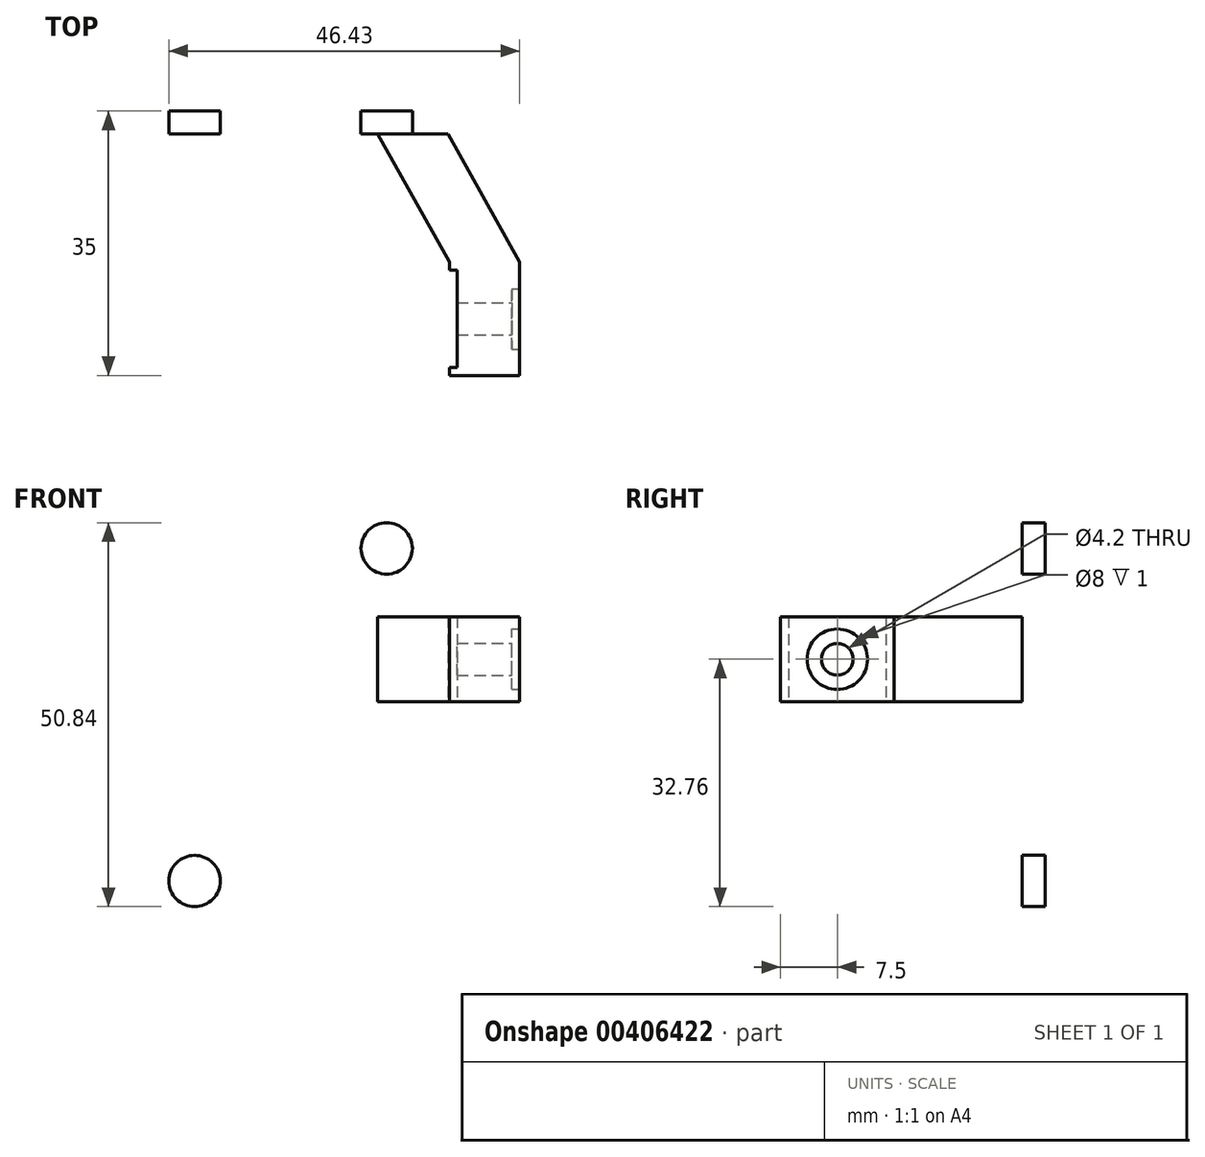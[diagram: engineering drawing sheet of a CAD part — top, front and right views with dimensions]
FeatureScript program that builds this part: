
annotation { "Feature Type Name" : "Feature", "Feature Type Description" : "" }
export const myFeature = defineFeature(function(context is Context, id is Id, definition is map)
    precondition{}
    {
        {
            var Q0;
            Q0=qCreatedBy(makeId("Front.planeOp"),FACE);
            var sketch = newSketch(context, id + "F0", { "sketchPlane" : qUnion([Q0])});
            skCircle(sketch, "E0", {"center": v(0, 0) * mm, "radius": 34 * mm});
            skCircle(sketch, "E1", {"center": v(0, 0) * mm, "radius": 24.25 * mm});
            skSolve(sketch);
        }
        {
            var Q0;
            Q0=makeQuery(id+"F0.imprint","IMPRINT",FACE,{"disambiguationData":[TD([[makeQuery(id+"F0.imprint","IMPRINT",EDGE,{"derivedFrom":sQuery(id+"F0.wireOp",EDGE,"E0")}),1.0]])]});
            extrude(context, id + "F1", {"entities" : qUnion([Q0]), "depth" : 3 * mm});
        }
        {
            var Q0;
            Q0=makeQuery(id+"F1.opExtrude","CAP_FACE",FACE,{"disambiguationData":[OSD([sQuery(id+"F0.wireOp",EDGE,"E0"),sQuery(id+"F0.wireOp",EDGE,"E1")])],"isStart":false});
            var sketch = newSketch(context, id + "F2", { "sketchPlane" : qUnion([Q0])});
            skCircle(sketch, "E2", {"center": v(0, 0) * mm, "radius": 29.36 * mm});
            skCircle(sketch, "E3", {"center": v(0, 29.36) * mm, "radius": 3.4 * mm});
            skCircle(sketch, "E4.1.0", {"center": v(-25.43, 14.68) * mm, "radius": 3.4 * mm});
            skCircle(sketch, "E4.2.0", {"center": v(-25.43, -14.68) * mm, "radius": 3.4 * mm});
            skCircle(sketch, "E4.3.0", {"center": v(0, -29.36) * mm, "radius": 3.4 * mm});
            skCircle(sketch, "E4.4.0", {"center": v(25.43, -14.68) * mm, "radius": 3.4 * mm});
            skCircle(sketch, "E4.5.0", {"center": v(25.43, 14.68) * mm, "radius": 3.4 * mm});
            skSolve(sketch);
        }
        {
            var Q0;
            {var subQ0=sQuery(id+"F2.wireOp",EDGE,"E3");var subQ1=sQuery(id+"F2.wireOp",EDGE,"E2");var subQ2=makeQuery(id+"F2.imprint","INTERSECT",VERTEX,{"disambiguationData":[OD(0.0)],"derivedFrom":[subQ1,subQ0]});Q0=makeQuery(id+"F2.imprint","IMPRINT",FACE,{"disambiguationData":[TD([[makeQuery(id+"F2.imprint","IMPRINT",EDGE,{"disambiguationData":[TD([[subQ2,-1.0]])],"derivedFrom":subQ1}),1.0]])]});}
            var Q1;
            {var subQ0=sQuery(id+"F2.wireOp",EDGE,"E3");var subQ1=sQuery(id+"F2.wireOp",EDGE,"E2");var subQ2=makeQuery(id+"F2.imprint","INTERSECT",VERTEX,{"disambiguationData":[OD(0.0)],"derivedFrom":[subQ1,subQ0]});Q1=makeQuery(id+"F2.imprint","IMPRINT",FACE,{"disambiguationData":[TD([[makeQuery(id+"F2.imprint","IMPRINT",EDGE,{"disambiguationData":[TD([[subQ2,-1.0]])],"derivedFrom":subQ1}),-1.0]])]});}
            var Q2;
            {var subQ0=sQuery(id+"F2.wireOp",EDGE,"E4.1.0");var subQ1=sQuery(id+"F2.wireOp",EDGE,"E2");var subQ2=makeQuery(id+"F2.imprint","INTERSECT",VERTEX,{"disambiguationData":[OD(0.0)],"derivedFrom":[subQ1,subQ0]});Q2=makeQuery(id+"F2.imprint","IMPRINT",FACE,{"disambiguationData":[TD([[makeQuery(id+"F2.imprint","IMPRINT",EDGE,{"disambiguationData":[TD([[subQ2,-1.0]])],"derivedFrom":subQ1}),1.0]])]});}
            var Q3;
            {var subQ0=sQuery(id+"F2.wireOp",EDGE,"E4.1.0");var subQ1=sQuery(id+"F2.wireOp",EDGE,"E2");var subQ2=makeQuery(id+"F2.imprint","INTERSECT",VERTEX,{"disambiguationData":[OD(0.0)],"derivedFrom":[subQ1,subQ0]});Q3=makeQuery(id+"F2.imprint","IMPRINT",FACE,{"disambiguationData":[TD([[makeQuery(id+"F2.imprint","IMPRINT",EDGE,{"disambiguationData":[TD([[subQ2,-1.0]])],"derivedFrom":subQ1}),-1.0]])]});}
            var Q4;
            {var subQ0=sQuery(id+"F2.wireOp",EDGE,"E4.2.0");var subQ1=sQuery(id+"F2.wireOp",EDGE,"E2");var subQ2=makeQuery(id+"F2.imprint","INTERSECT",VERTEX,{"disambiguationData":[OD(0.0)],"derivedFrom":[subQ1,subQ0]});Q4=makeQuery(id+"F2.imprint","IMPRINT",FACE,{"disambiguationData":[TD([[makeQuery(id+"F2.imprint","IMPRINT",EDGE,{"disambiguationData":[TD([[subQ2,-1.0]])],"derivedFrom":subQ1}),1.0]])]});}
            var Q5;
            {var subQ0=sQuery(id+"F2.wireOp",EDGE,"E4.2.0");var subQ1=sQuery(id+"F2.wireOp",EDGE,"E2");var subQ2=makeQuery(id+"F2.imprint","INTERSECT",VERTEX,{"disambiguationData":[OD(0.0)],"derivedFrom":[subQ1,subQ0]});Q5=makeQuery(id+"F2.imprint","IMPRINT",FACE,{"disambiguationData":[TD([[makeQuery(id+"F2.imprint","IMPRINT",EDGE,{"disambiguationData":[TD([[subQ2,-1.0]])],"derivedFrom":subQ1}),-1.0]])]});}
            var Q6;
            {var subQ0=sQuery(id+"F2.wireOp",EDGE,"E4.5.0");var subQ1=sQuery(id+"F2.wireOp",EDGE,"E2");var subQ2=makeQuery(id+"F2.imprint","INTERSECT",VERTEX,{"disambiguationData":[OD(0.0)],"derivedFrom":[subQ1,subQ0]});Q6=makeQuery(id+"F2.imprint","IMPRINT",FACE,{"disambiguationData":[TD([[makeQuery(id+"F2.imprint","IMPRINT",EDGE,{"disambiguationData":[TD([[subQ2,1.0]])],"derivedFrom":subQ1}),-1.0]])]});}
            var Q7;
            {var subQ0=sQuery(id+"F2.wireOp",EDGE,"E4.5.0");var subQ1=sQuery(id+"F2.wireOp",EDGE,"E2");var subQ2=makeQuery(id+"F2.imprint","INTERSECT",VERTEX,{"disambiguationData":[OD(0.0)],"derivedFrom":[subQ1,subQ0]});Q7=makeQuery(id+"F2.imprint","IMPRINT",FACE,{"disambiguationData":[TD([[makeQuery(id+"F2.imprint","IMPRINT",EDGE,{"disambiguationData":[TD([[subQ2,1.0]])],"derivedFrom":subQ1}),1.0]])]});}
            var Q8;
            {var subQ0=sQuery(id+"F2.wireOp",EDGE,"E4.4.0");var subQ1=sQuery(id+"F2.wireOp",EDGE,"E2");var subQ2=makeQuery(id+"F2.imprint","INTERSECT",VERTEX,{"disambiguationData":[OD(0.0)],"derivedFrom":[subQ1,subQ0]});Q8=makeQuery(id+"F2.imprint","IMPRINT",FACE,{"disambiguationData":[TD([[makeQuery(id+"F2.imprint","IMPRINT",EDGE,{"disambiguationData":[TD([[subQ2,-1.0]])],"derivedFrom":subQ1}),-1.0]])]});}
            var Q9;
            {var subQ0=sQuery(id+"F2.wireOp",EDGE,"E4.4.0");var subQ1=sQuery(id+"F2.wireOp",EDGE,"E2");var subQ2=makeQuery(id+"F2.imprint","INTERSECT",VERTEX,{"disambiguationData":[OD(0.0)],"derivedFrom":[subQ1,subQ0]});Q9=makeQuery(id+"F2.imprint","IMPRINT",FACE,{"disambiguationData":[TD([[makeQuery(id+"F2.imprint","IMPRINT",EDGE,{"disambiguationData":[TD([[subQ2,-1.0]])],"derivedFrom":subQ1}),1.0]])]});}
            var Q10;
            {var subQ0=sQuery(id+"F2.wireOp",EDGE,"E4.3.0");var subQ1=sQuery(id+"F2.wireOp",EDGE,"E2");var subQ2=makeQuery(id+"F2.imprint","INTERSECT",VERTEX,{"disambiguationData":[OD(0.0)],"derivedFrom":[subQ1,subQ0]});Q10=makeQuery(id+"F2.imprint","IMPRINT",FACE,{"disambiguationData":[TD([[makeQuery(id+"F2.imprint","IMPRINT",EDGE,{"disambiguationData":[TD([[subQ2,-1.0]])],"derivedFrom":subQ1}),-1.0]])]});}
            var Q11;
            {var subQ0=sQuery(id+"F2.wireOp",EDGE,"E4.3.0");var subQ1=sQuery(id+"F2.wireOp",EDGE,"E2");var subQ2=makeQuery(id+"F2.imprint","INTERSECT",VERTEX,{"disambiguationData":[OD(0.0)],"derivedFrom":[subQ1,subQ0]});Q11=makeQuery(id+"F2.imprint","IMPRINT",FACE,{"disambiguationData":[TD([[makeQuery(id+"F2.imprint","IMPRINT",EDGE,{"disambiguationData":[TD([[subQ2,-1.0]])],"derivedFrom":subQ1}),1.0]])]});}
            extrude(context, id + "F3", {"entities" : qUnion([Q0, Q1, Q2, Q3, Q4, Q5, Q6, Q7, Q8, Q9, Q10, Q11]), "operationType" : NewBodyOperationType.REMOVE, "endBound" : BoundingType.UP_TO_NEXT, "oppositeDirection" : true, "depth" : 25 * mm});
        }
        {
            var Q0;
            Q0=makeQuery(id+"F1.opExtrude","CAP_FACE",FACE,{"disambiguationData":[OSD([sQuery(id+"F0.wireOp",EDGE,"E0"),sQuery(id+"F0.wireOp",EDGE,"E1")])],"isStart":false});
            var sketch = newSketch(context, id + "F4", { "sketchPlane" : qUnion([Q0])});
            skLineSegment(sketch, "E5.bottom", {"start": v(24.25, 5.64) * mm, "end": v(33.53, 5.64) * mm});
            skLineSegment(sketch, "E5.top", {"start": v(24.25, -5.64) * mm, "end": v(33.53, -5.64) * mm});
            skLineSegment(sketch, "E5.left", {"start": v(24.25, 5.64) * mm, "end": v(24.25, -5.64) * mm});
            skLineSegment(sketch, "E5.right", {"start": v(33.53, 5.64) * mm, "end": v(33.53, -5.64) * mm});
            skPoint(sketch, "E5.middle", {"position": v(28.89, 0) * mm});
            skSolve(sketch);
        }
        {
            var Q0;
            Q0=qCreatedBy(makeId("Top.planeOp"),FACE);
            var sketch = newSketch(context, id + "F5", { "sketchPlane" : qUnion([Q0])});
            skLineSegment(sketch, "E6", {"start": v(24.25, -3) * mm, "end": v(33.75, -20) * mm});
            skSolve(sketch);
        }
        {
            var Q0;
            {var subQ3=sQuery(id+"F4.wireOp",EDGE,"E5.bottom");Q0=makeQuery(id+"F4.imprint","IMPRINT",FACE,{"disambiguationData":[TD([[makeQuery(id+"F4.imprint","IMPRINT",EDGE,{"derivedFrom":subQ3}),-1.0]])]});}
            var Q1;
            Q1=qConstructionFilter(qBodyType(qCreatedBy(id+"F5",EDGE),BodyType.WIRE),ConstructionObject.NO);
            sweep(context, id + "F6", {"operationType" : NewBodyOperationType.ADD, "profiles" : qUnion([Q0]), "path" : qUnion([Q1])});
        }
        {
            var Q0;
            Q0=makeQuery(id+"F6.opSweep","CAP_FACE",FACE,{"disambiguationData":[OSD([sQuery(id+"F4.wireOp",EDGE,"E5.bottom"),sQuery(id+"F4.wireOp",EDGE,"E5.top"),sQuery(id+"F4.wireOp",EDGE,"E5.left"),sQuery(id+"F4.wireOp",EDGE,"E5.right"),sQuery(id+"F5.wireOp",VERTEX,"E6.end")])],"isStart":false});
            extrude(context, id + "F7", {"entities" : qUnion([Q0]), "operationType" : NewBodyOperationType.ADD, "depth" : 15 * mm});
        }
        {
            var Q0;
            Q0=makeQuery(id+"F7.opExtrude","SWEPT_FACE",FACE,{"disambiguationData":[OSD([sQuery(id+"F4.wireOp",EDGE,"E5.right"),sQuery(id+"F5.wireOp",VERTEX,"E6.end")])]});
            var sketch = newSketch(context, id + "F8", { "sketchPlane" : qUnion([Q0])});
            skLineSegment(sketch, "E7", {"start": v(-35, -5.64) * mm, "end": v(-20, 5.64) * mm});
            skLineSegment(sketch, "E8", {"start": v(-20, 5.64) * mm, "end": v(-35, 5.64) * mm});
            skLineSegment(sketch, "E9", {"start": v(-35, 5.64) * mm, "end": v(-20, -5.64) * mm});
            skCircle(sketch, "E10", {"center": v(-27.5, 0) * mm, "radius": 2.1 * mm});
            skCircle(sketch, "E11", {"center": v(-27.5, 0) * mm, "radius": 4 * mm});
            skSolve(sketch);
        }
        {
            var Q0;
            {var subQ0=sQuery(id+"F8.wireOp",EDGE,"E9");var subQ1=sQuery(id+"F8.wireOp",EDGE,"E7");var subQ2=makeQuery(id+"F8.imprint","INTERSECT",VERTEX,{"derivedFrom":[subQ1,subQ0]});Q0=makeQuery(id+"F8.imprint","IMPRINT",FACE,{"disambiguationData":[TD([[makeQuery(id+"F8.imprint","IMPRINT",EDGE,{"disambiguationData":[TD([[subQ2,-1.0]])],"derivedFrom":subQ1}),1.0]])]});}
            var Q1;
            {var subQ0=sQuery(id+"F8.wireOp",EDGE,"E10");var subQ1=sQuery(id+"F8.wireOp",EDGE,"E7");var subQ2=makeQuery(id+"F8.imprint","INTERSECT",VERTEX,{"disambiguationData":[OD(0.0)],"derivedFrom":[subQ1,subQ0]});Q1=makeQuery(id+"F8.imprint","IMPRINT",FACE,{"disambiguationData":[TD([[makeQuery(id+"F8.imprint","IMPRINT",EDGE,{"disambiguationData":[TD([[subQ2,-1.0]])],"derivedFrom":subQ1}),1.0]])]});}
            var Q2;
            {var subQ0=sQuery(id+"F8.wireOp",EDGE,"E9");var subQ1=sQuery(id+"F8.wireOp",EDGE,"E7");var subQ2=makeQuery(id+"F8.imprint","INTERSECT",VERTEX,{"derivedFrom":[subQ1,subQ0]});Q2=makeQuery(id+"F8.imprint","IMPRINT",FACE,{"disambiguationData":[TD([[makeQuery(id+"F8.imprint","IMPRINT",EDGE,{"disambiguationData":[TD([[subQ2,-1.0]])],"derivedFrom":subQ1}),-1.0]])]});}
            var Q3;
            {var subQ0=sQuery(id+"F8.wireOp",EDGE,"E10");var subQ1=sQuery(id+"F8.wireOp",EDGE,"E7");var subQ2=makeQuery(id+"F8.imprint","INTERSECT",VERTEX,{"disambiguationData":[OD(0.0)],"derivedFrom":[subQ1,subQ0]});Q3=makeQuery(id+"F8.imprint","IMPRINT",FACE,{"disambiguationData":[TD([[makeQuery(id+"F8.imprint","IMPRINT",EDGE,{"disambiguationData":[TD([[subQ2,-1.0]])],"derivedFrom":subQ1}),-1.0]])]});}
            extrude(context, id + "F9", {"entities" : qUnion([Q0, Q1, Q2, Q3]), "operationType" : NewBodyOperationType.REMOVE, "endBound" : BoundingType.UP_TO_NEXT, "oppositeDirection" : true, "depth" : 25 * mm});
        }
        {
            var Q0;
            {var subQ0=sQuery(id+"F8.wireOp",EDGE,"E10");var subQ1=sQuery(id+"F8.wireOp",EDGE,"E7");var subQ2=makeQuery(id+"F8.imprint","INTERSECT",VERTEX,{"disambiguationData":[OD(1.0)],"derivedFrom":[subQ1,subQ0]});Q0=makeQuery(id+"F8.imprint","IMPRINT",FACE,{"disambiguationData":[TD([[makeQuery(id+"F8.imprint","IMPRINT",EDGE,{"disambiguationData":[TD([[subQ2,-1.0]])],"derivedFrom":subQ1}),1.0]])]});}
            var Q1;
            {var subQ0=sQuery(id+"F8.wireOp",EDGE,"E11");var subQ1=sQuery(id+"F8.wireOp",EDGE,"E7");var subQ2=makeQuery(id+"F8.imprint","INTERSECT",VERTEX,{"disambiguationData":[OD(0.0)],"derivedFrom":[subQ1,subQ0]});Q1=makeQuery(id+"F8.imprint","IMPRINT",FACE,{"disambiguationData":[TD([[makeQuery(id+"F8.imprint","IMPRINT",EDGE,{"disambiguationData":[TD([[subQ2,-1.0]])],"derivedFrom":subQ1}),1.0]])]});}
            var Q2;
            {var subQ0=sQuery(id+"F8.wireOp",EDGE,"E11");var subQ1=sQuery(id+"F8.wireOp",EDGE,"E7");var subQ2=makeQuery(id+"F8.imprint","INTERSECT",VERTEX,{"disambiguationData":[OD(0.0)],"derivedFrom":[subQ1,subQ0]});Q2=makeQuery(id+"F8.imprint","IMPRINT",FACE,{"disambiguationData":[TD([[makeQuery(id+"F8.imprint","IMPRINT",EDGE,{"disambiguationData":[TD([[subQ2,-1.0]])],"derivedFrom":subQ1}),-1.0]])]});}
            var Q3;
            {var subQ0=sQuery(id+"F8.wireOp",EDGE,"E10");var subQ1=sQuery(id+"F8.wireOp",EDGE,"E7");var subQ2=makeQuery(id+"F8.imprint","INTERSECT",VERTEX,{"disambiguationData":[OD(1.0)],"derivedFrom":[subQ1,subQ0]});Q3=makeQuery(id+"F8.imprint","IMPRINT",FACE,{"disambiguationData":[TD([[makeQuery(id+"F8.imprint","IMPRINT",EDGE,{"disambiguationData":[TD([[subQ2,-1.0]])],"derivedFrom":subQ1}),-1.0]])]});}
            extrude(context, id + "F10", {"entities" : qUnion([Q0, Q1, Q2, Q3]), "operationType" : NewBodyOperationType.REMOVE, "oppositeDirection" : true, "depth" : 1 * mm});
        }
        {
            var Q0;
            Q0=makeQuery(id+"F7.opExtrude","SWEPT_FACE",FACE,{"disambiguationData":[OSD([sQuery(id+"F4.wireOp",EDGE,"E5.left"),sQuery(id+"F5.wireOp",VERTEX,"E6.end")])]});
            var sketch = newSketch(context, id + "F11", { "sketchPlane" : qUnion([Q0])});
            skLineSegment(sketch, "E12.bottom", {"start": v(21.05, 5.64) * mm, "end": v(33.95, 5.64) * mm});
            skLineSegment(sketch, "E12.top", {"start": v(21.05, -5.64) * mm, "end": v(33.95, -5.64) * mm});
            skLineSegment(sketch, "E12.left", {"start": v(21.05, 5.64) * mm, "end": v(21.05, -5.64) * mm});
            skLineSegment(sketch, "E12.right", {"start": v(33.95, 5.64) * mm, "end": v(33.95, -5.64) * mm});
            skPoint(sketch, "E12.middle", {"position": v(27.5, 0) * mm});
            skSolve(sketch);
        }
        {
            var Q0;
            Q0=makeQuery(id+"F11.imprint","IMPRINT",FACE,{"disambiguationData":[TD([[makeQuery(id+"F11.imprint","IMPRINT",EDGE,{"derivedFrom":sQuery(id+"F11.wireOp",EDGE,"E12.bottom")}),1.0]])]});
            extrude(context, id + "F12", {"entities" : qUnion([Q0]), "operationType" : NewBodyOperationType.REMOVE, "oppositeDirection" : true, "depth" : 1 * mm});
        }
        {
            var Q0;
            Q0=makeQuery(id+"F1.opExtrude","CAP_FACE",FACE,{"disambiguationData":[OSD([sQuery(id+"F0.wireOp",EDGE,"E0"),sQuery(id+"F0.wireOp",EDGE,"E1")])],"isStart":true});
            var sketch = newSketch(context, id + "F13", { "sketchPlane" : qUnion([Q0])});
            skLineSegment(sketch, "E13.bottom", {"start": v(-15, -55.78) * mm, "end": v(51.04, -55.78) * mm});
            skLineSegment(sketch, "E13.top", {"start": v(-15, 40.26) * mm, "end": v(51.04, 40.26) * mm});
            skLineSegment(sketch, "E13.left", {"start": v(-15, -55.78) * mm, "end": v(-15, 40.26) * mm});
            skLineSegment(sketch, "E13.right", {"start": v(51.04, -55.78) * mm, "end": v(51.04, 40.26) * mm});
            skSolve(sketch);
        }
        {
            var Q0;
            {var subQ1=sQuery(id+"F13.wireOp",EDGE,"E13.bottom");Q0=makeQuery(id+"F13.imprint","IMPRINT",FACE,{"disambiguationData":[TD([[makeQuery(id+"F13.imprint","IMPRINT",EDGE,{"derivedFrom":subQ1}),1.0]])]});}
            var Q1;
            {var subQ0=sQuery(id+"F13.wireOp",EDGE,"E13.left");var subQ1=makeQuery(id+"F1.opExtrude","CAP_EDGE",EDGE,{"disambiguationData":[OSD([sQuery(id+"F0.wireOp",EDGE,"E1")])],"isStart":true});var subQ2=makeQuery(id+"F13.imprint","INTERSECT",VERTEX,{"disambiguationData":[OD(0.0)],"derivedFrom":[subQ1,subQ0]});Q1=makeQuery(id+"F13.imprint","IMPRINT",FACE,{"disambiguationData":[TD([[makeQuery(id+"F13.imprint","IMPRINT",EDGE,{"disambiguationData":[TD([[subQ2,-1.0]])],"derivedFrom":subQ0}),-1.0]])]});}
            var Q2;
            {var subQ5=sQuery(id+"F0.wireOp",EDGE,"E0");var subQ7=sQuery(id+"F13.wireOp",EDGE,"E13.left");var subQ8=makeQuery(id+"F1.opExtrude","CAP_EDGE",EDGE,{"disambiguationData":[OSD([subQ5])],"isStart":true});var subQ15=makeQuery(id+"F13.imprint","INTERSECT",VERTEX,{"disambiguationData":[OD(0.0)],"derivedFrom":[subQ8,subQ7]});Q2=makeQuery(id+"F13.imprint","IMPRINT",FACE,{"disambiguationData":[TD([[makeQuery(id+"F13.imprint","IMPRINT",EDGE,{"disambiguationData":[TD([[subQ15,-1.0]])],"derivedFrom":subQ7}),-1.0]])]});}
            extrude(context, id + "F14", {"entities" : qUnion([Q0, Q1, Q2]), "operationType" : NewBodyOperationType.REMOVE, "oppositeDirection" : true, "depth" : 25 * mm});
        }
    });
